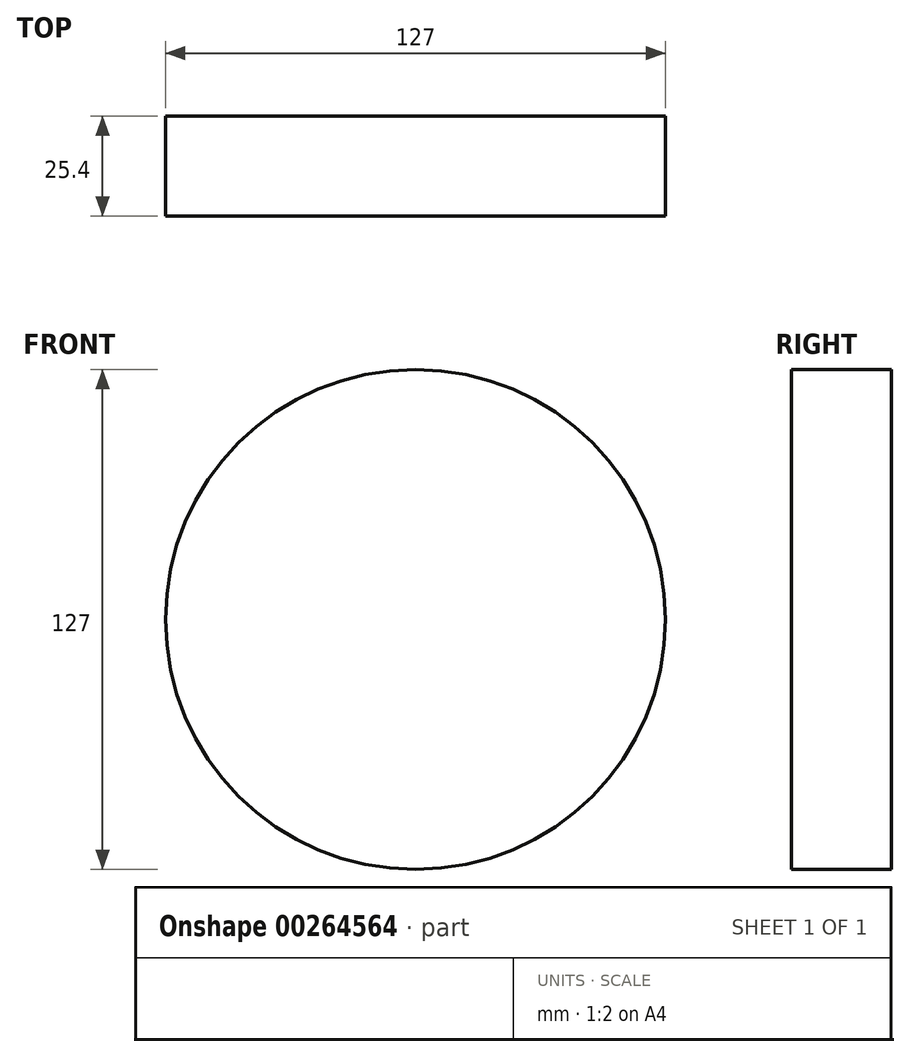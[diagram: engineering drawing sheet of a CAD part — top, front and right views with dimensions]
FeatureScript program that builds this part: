
annotation { "Feature Type Name" : "Feature", "Feature Type Description" : "" }
export const myFeature = defineFeature(function(context is Context, id is Id, definition is map)
    precondition{}
    {
        {
            var Q0;
            Q0=qCreatedBy(makeId("Front.planeOp"),FACE);
            var sketch = newSketch(context, id + "F0", { "sketchPlane" : qUnion([Q0])});
            skCircle(sketch, "E0", {"center": v(0, 0) * mm, "radius": 63.5 * mm});
            skSolve(sketch);
        }
        {
            var Q0;
            Q0 = qSketchRegion(id + "F0", true);
            extrude(context, id + "F1", {"entities" : qUnion([Q0]), "depth" : 25.4 * mm});
        }
    });
